# Revit family: xSoap_Dispenser-DXV-Contemporary-D35401720_Series
name_source: partatom
category: Specialty Equipment
revit_build: Autodesk Revit 2014 (Build: 20130308_1515(x64)
units: mm (PartAtom-declared; Revit-internal decimal feet)

## types (2) — shared parameters
Assembly Code = C1030220
Description = Contemporary Soap Dispenser
Height = 2 3/4"
Installation Type = Deck Mounted
Length = 4 7/8"
Manufacturer = DXV
Price = Prices may vary. Please consult Manufacturer Representative for most up-to-date price list.
Product Documentation Link = http://dxv.blob.core.windows.net
Product Page URL = http://www.dxv.com
URL = http://www.dxv.com
Warranty Information = Lifetime Limited Warranty
Width = 1 3/4"

## per-type parameters (varying)
| type | Body | Material |
| D35401720.100 | Metal-DXV-100-Polished Chrome | Metal-DXV-100-Polished Chrome |
| D35401720.355 | Metal-DXV-355-Ultra Steel | Metal-DXV-355-Ultra Steel |

note: column(s) folded — value = type name in every type: Model

## geometry (parser evidence)
native form markers: Sweep x1
no freeform markers — native parametric forms only
